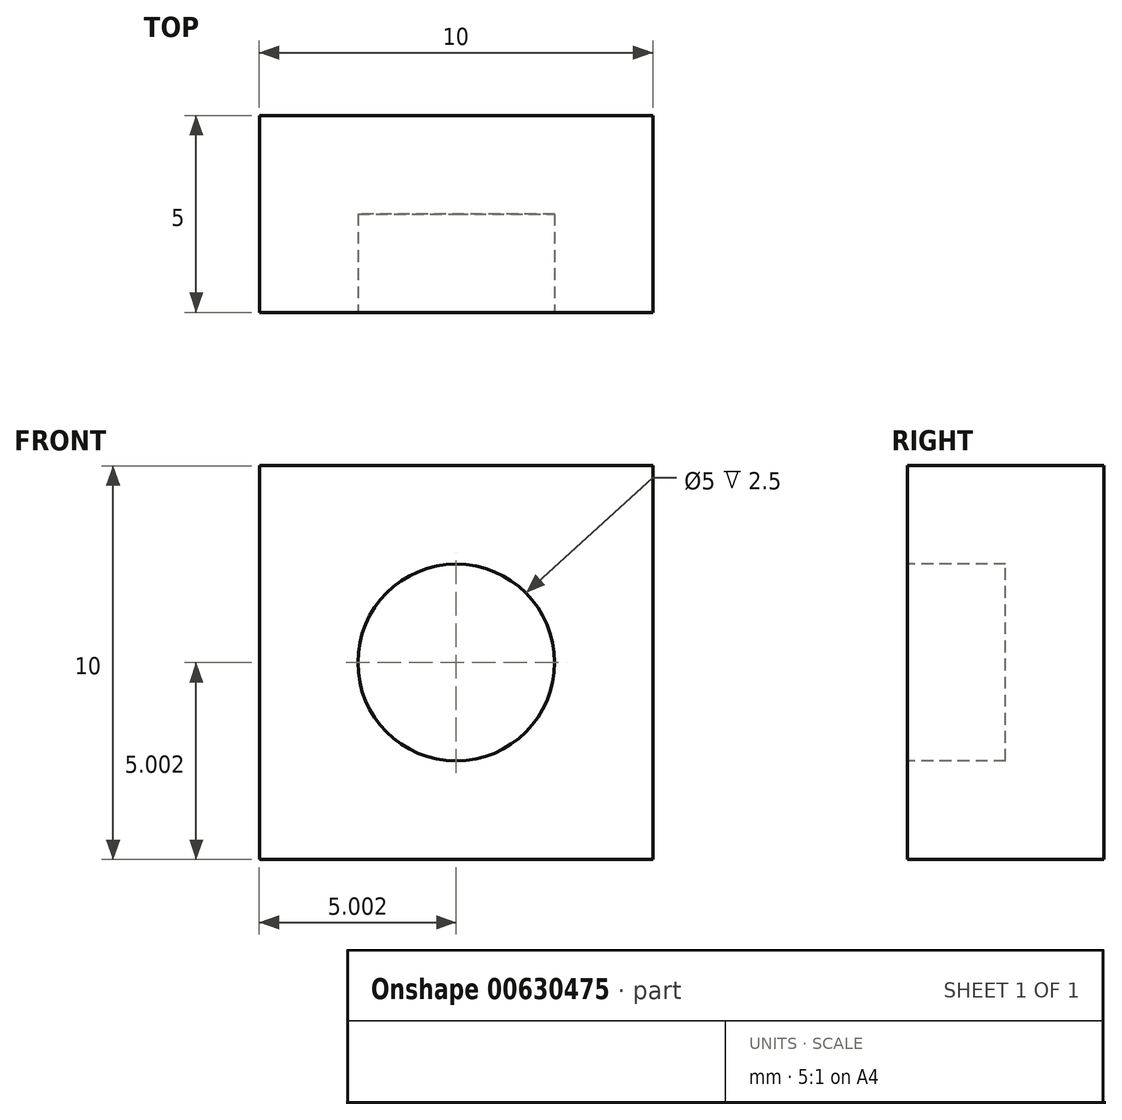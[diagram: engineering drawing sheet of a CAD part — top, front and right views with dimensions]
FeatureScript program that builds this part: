
annotation { "Feature Type Name" : "Feature", "Feature Type Description" : "" }
export const myFeature = defineFeature(function(context is Context, id is Id, definition is map)
    precondition{}
    {
        {
            var Q0;
            Q0=qCreatedBy(makeId("Front.planeOp"),FACE);
            var sketch = newSketch(context, id + "F0", { "sketchPlane" : qUnion([Q0])});
            skLineSegment(sketch, "E0.bottom", {"start": v(22.24, 17.85) * mm, "end": v(32.24, 17.85) * mm});
            skLineSegment(sketch, "E0.top", {"start": v(22.24, 27.85) * mm, "end": v(32.24, 27.85) * mm});
            skLineSegment(sketch, "E0.left", {"start": v(22.24, 17.85) * mm, "end": v(22.24, 27.85) * mm});
            skLineSegment(sketch, "E0.right", {"start": v(32.24, 17.85) * mm, "end": v(32.24, 27.85) * mm});
            skSolve(sketch);
        }
        {
            var Q0;
            Q0 = qSketchRegion(id + "F0", true);
            extrude(context, id + "F1", {"entities" : qUnion([Q0]), "depth" : 5 * mm, "offsetDistance" : 25 * mm});
        }
        {
            var Q0;
            Q0=makeQuery(id+"F1.opExtrude","CAP_FACE",FACE,{"disambiguationData":[OSD([sQuery(id+"F0.wireOp",EDGE,"E0.bottom"),sQuery(id+"F0.wireOp",EDGE,"E0.top"),sQuery(id+"F0.wireOp",EDGE,"E0.left"),sQuery(id+"F0.wireOp",EDGE,"E0.right")])],"isStart":false});
            var sketch = newSketch(context, id + "F2", { "sketchPlane" : qUnion([Q0])});
            skCircle(sketch, "E1", {"center": v(27.24, 22.85) * mm, "radius": 2.5 * mm});
            skPoint(sketch, "E1.centerSnap0", {"position": v(22.24, 22.85) * mm});
            skPoint(sketch, "E1.centerSnap1", {"position": v(27.24, 27.85) * mm});
            skSolve(sketch);
        }
        {
            var Q0;
            Q0 = qSketchRegion(id + "F2", true);
            extrude(context, id + "F3", {"entities" : qUnion([Q0]), "operationType" : NewBodyOperationType.REMOVE, "oppositeDirection" : true, "depth" : 2.5 * mm, "offsetDistance" : 25 * mm});
        }
    });
